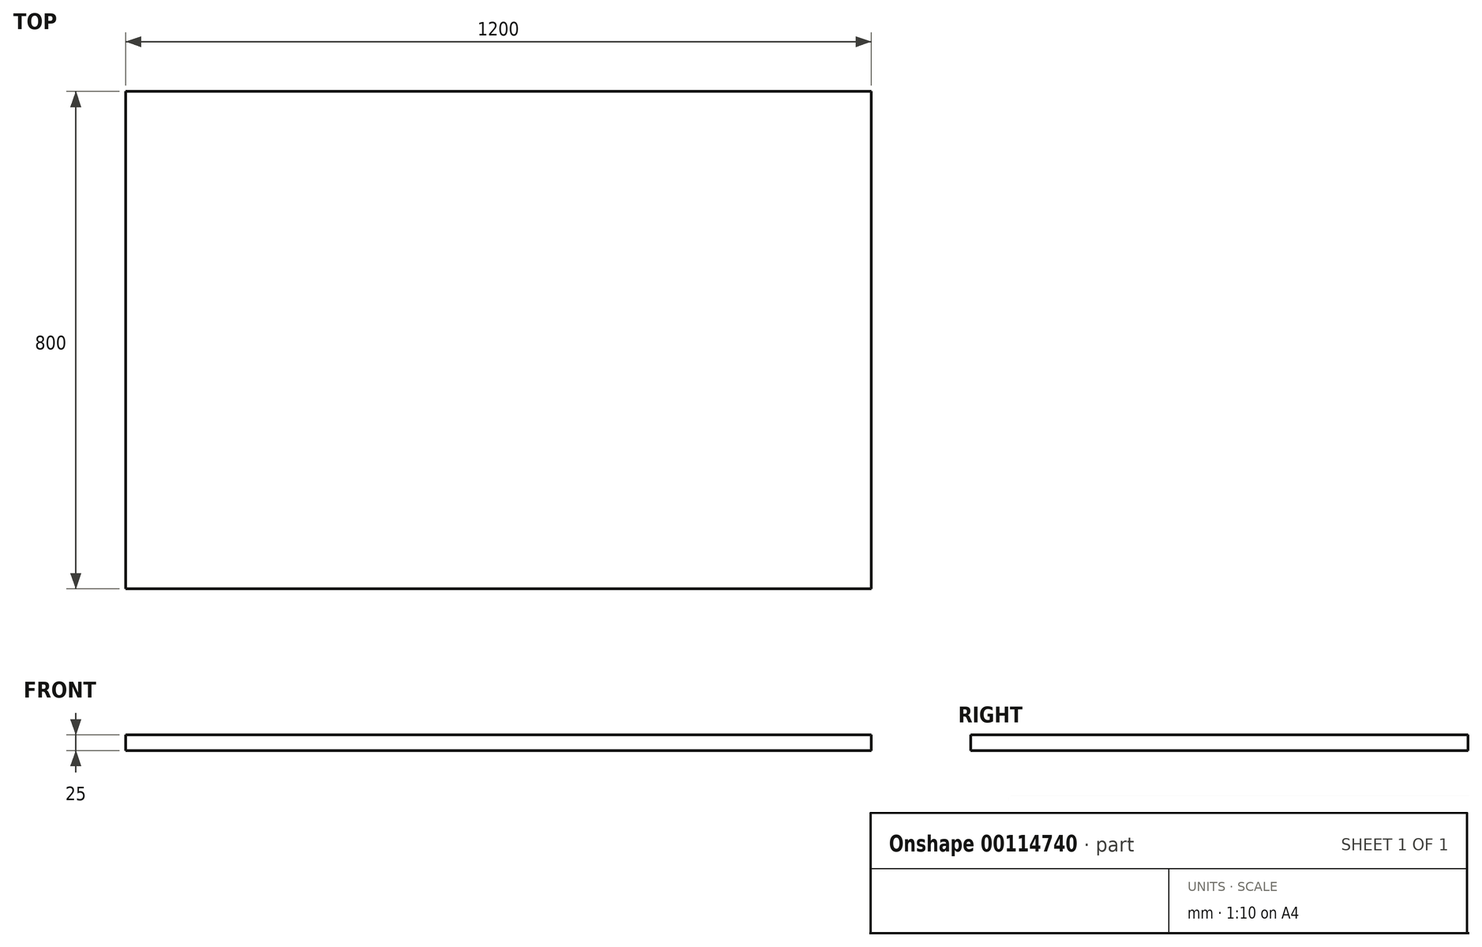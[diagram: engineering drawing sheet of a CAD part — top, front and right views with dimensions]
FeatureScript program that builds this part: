
annotation { "Feature Type Name" : "Feature", "Feature Type Description" : "" }
export const myFeature = defineFeature(function(context is Context, id is Id, definition is map)
    precondition{}
    {
        {
            var Q0;
            Q0=qCreatedBy(makeId("Top.planeOp"),FACE);
            var sketch = newSketch(context, id + "F0", { "sketchPlane" : qUnion([Q0])});
            skLineSegment(sketch, "E0.bottom", {"start": v(-600, 400) * mm, "end": v(600, 400) * mm});
            skLineSegment(sketch, "E0.top", {"start": v(-600, -400) * mm, "end": v(600, -400) * mm});
            skLineSegment(sketch, "E0.left", {"start": v(-600, 400) * mm, "end": v(-600, -400) * mm});
            skLineSegment(sketch, "E0.right", {"start": v(600, 400) * mm, "end": v(600, -400) * mm});
            skPoint(sketch, "E0.middle", {"position": v(0, 0) * mm});
            skSolve(sketch);
        }
        {
            var Q0;
            Q0=makeQuery(id+"F0.imprint","IMPRINT",FACE,{"disambiguationData":[TD([[makeQuery(id+"F0.imprint","IMPRINT",EDGE,{"derivedFrom":sQuery(id+"F0.wireOp",EDGE,"E0.bottom")}),-1.0]])]});
            extrude(context, id + "F1", {"entities" : qUnion([Q0]), "oppositeDirection" : true, "depth" : 25 * mm});
        }
    });
